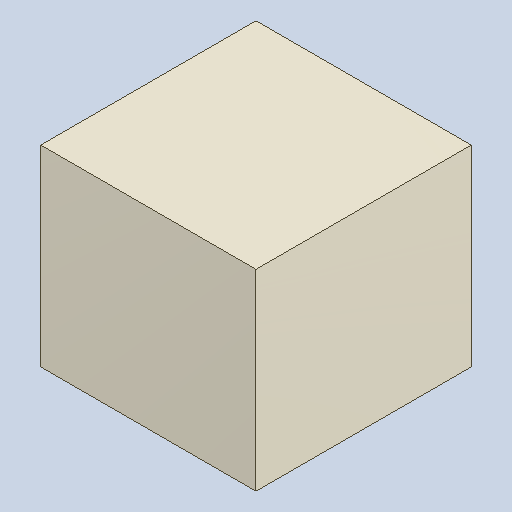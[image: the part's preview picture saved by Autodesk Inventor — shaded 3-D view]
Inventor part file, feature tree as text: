
AUTODESK INVENTOR PART (.ipt)
format: ipt  version: 2023.4 (Build 274418000, 418)  size: 81,920 bytes
history: native  units: mm
features: extrude x1
ambient origin geometry x8: Origin, YZ Plane, XZ Plane, XY Plane, X Axis, Y Axis, Z Axis, Center Point
bodies: Solid1 (feature_tree)
feature tree (1):
  extrude  "Extruded_7"  [1 undecoded]
note: 1 required parameter value undecoded (feature->parameter linkage not recoverable at this tier; creation-order binding heuristic only, values carry confidence <= 0.55)
